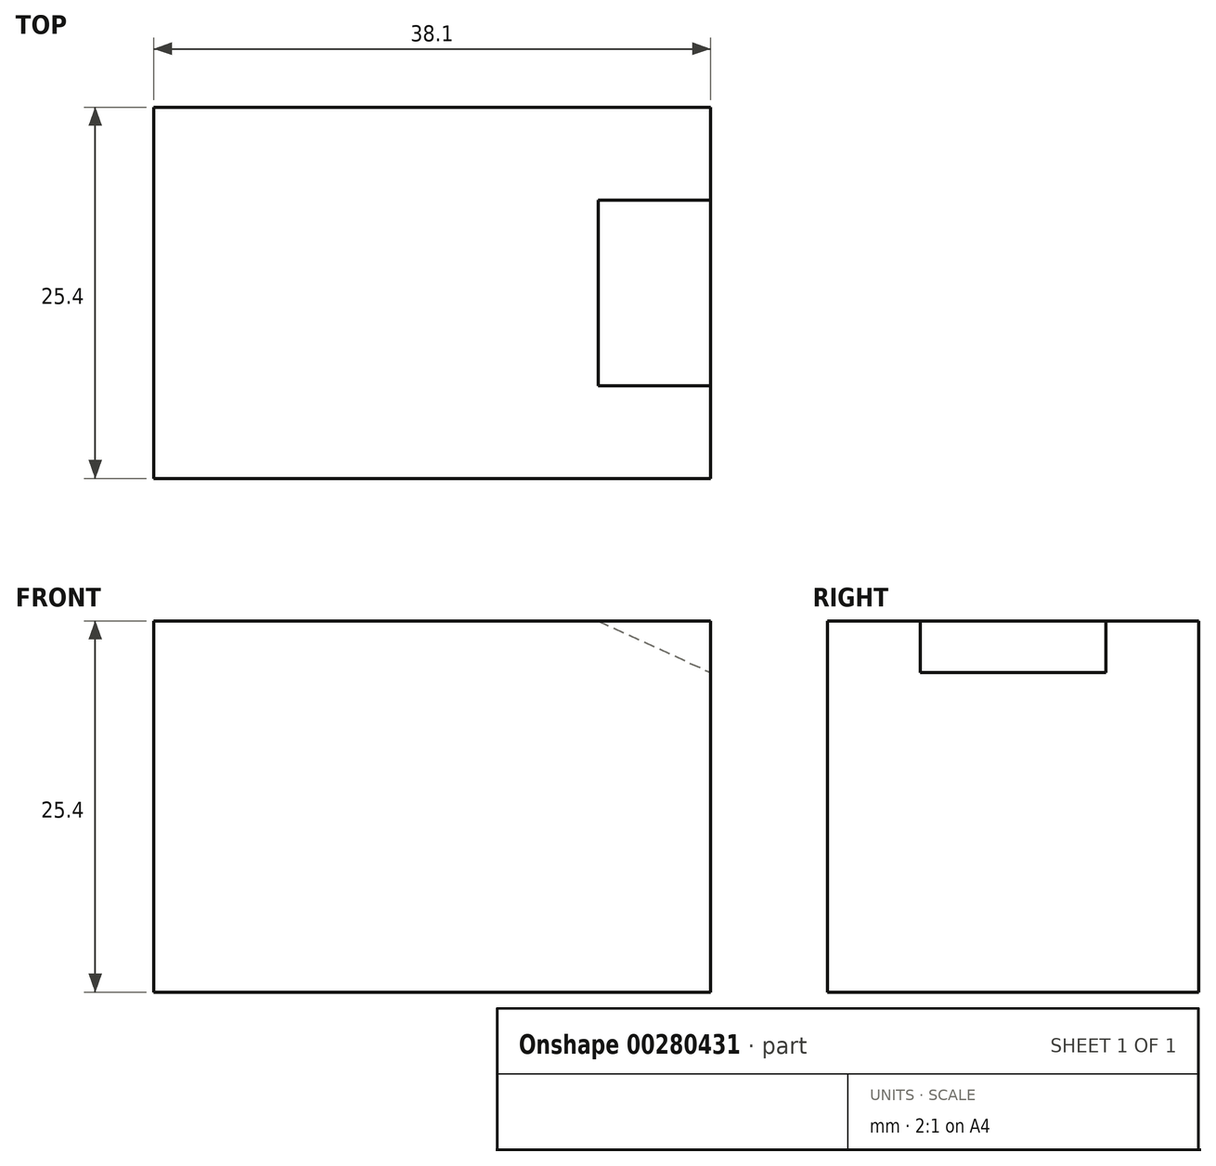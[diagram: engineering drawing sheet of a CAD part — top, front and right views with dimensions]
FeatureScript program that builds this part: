
annotation { "Feature Type Name" : "Feature", "Feature Type Description" : "" }
export const myFeature = defineFeature(function(context is Context, id is Id, definition is map)
    precondition{}
    {
        {
            var Q0;
            Q0=qCreatedBy(makeId("Front.planeOp"),FACE);
            var sketch = newSketch(context, id + "F0", { "sketchPlane" : qUnion([Q0])});
            skLineSegment(sketch, "E0", {"start": v(0, 0) * mm, "end": v(38.1, 0) * mm});
            skLineSegment(sketch, "E1", {"start": v(38.1, 0) * mm, "end": v(38.1, 25.4) * mm});
            skLineSegment(sketch, "E2", {"start": v(38.1, 25.4) * mm, "end": v(0, 25.4) * mm});
            skLineSegment(sketch, "E3", {"start": v(0, 25.4) * mm, "end": v(0, 0) * mm});
            skSolve(sketch);
        }
        {
            var Q0;
            Q0 = qSketchRegion(id + "F0", true);
            extrude(context, id + "F1", {"entities" : qUnion([Q0]), "endBound" : BoundingType.SYMMETRIC, "depth" : 25.4 * mm});
        }
        {
            var Q0;
            Q0=makeQuery(id+"F0.imprint","IMPRINT",FACE,{"disambiguationData":[TD([[makeQuery(id+"F0.imprint","IMPRINT",EDGE,{"derivedFrom":sQuery(id+"F0.wireOp",EDGE,"E0")}),1.0]])]});
            var sketch = newSketch(context, id + "F2", { "sketchPlane" : qUnion([Q0])});
            skLineSegment(sketch, "E4", {"start": v(38.1, 25.4) * mm, "end": v(30.42, 25.4) * mm});
            skLineSegment(sketch, "E5", {"start": v(30.42, 25.4) * mm, "end": v(38.1, 21.86) * mm});
            skLineSegment(sketch, "E6", {"start": v(38.1, 21.86) * mm, "end": v(38.1, 25.4) * mm});
            skSolve(sketch);
        }
        {
            var Q0;
            Q0 = qSketchRegion(id + "F2", true);
            extrude(context, id + "F3", {"entities" : qUnion([Q0]), "operationType" : NewBodyOperationType.REMOVE, "endBound" : BoundingType.SYMMETRIC, "depth" : 12.7 * mm});
        }
    });
